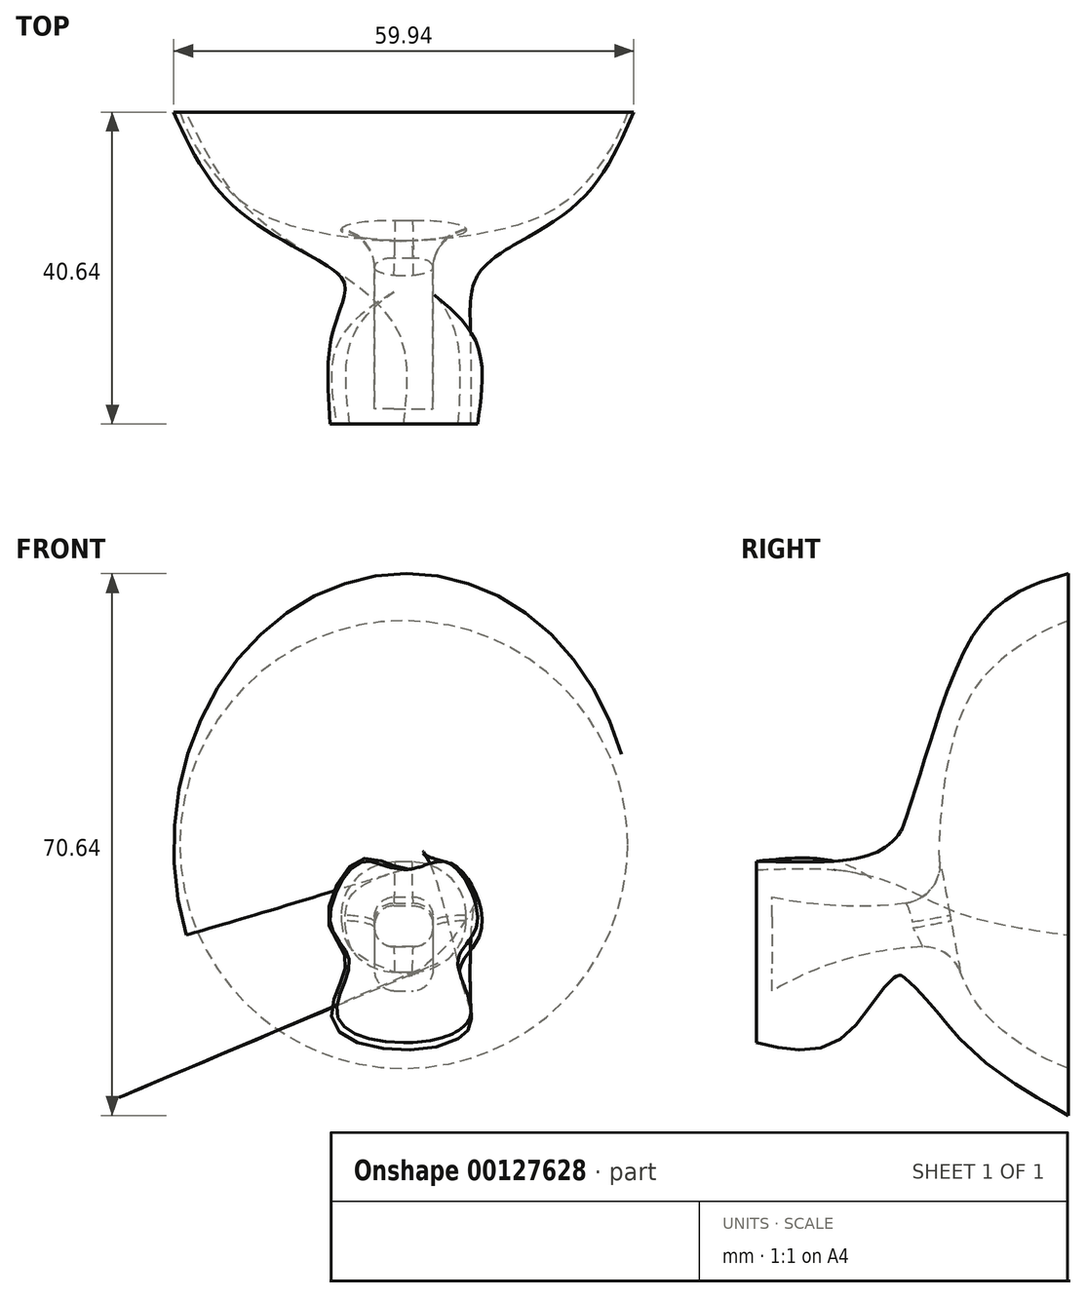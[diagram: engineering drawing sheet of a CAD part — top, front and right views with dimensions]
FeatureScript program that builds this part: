
annotation { "Feature Type Name" : "Feature", "Feature Type Description" : "" }
export const myFeature = defineFeature(function(context is Context, id is Id, definition is map)
    precondition{}
    {
        {
            var Q0;
            Q0=qCreatedBy(makeId("Front.planeOp"),FACE);
            var sketch = newSketch(context, id + "F0", { "sketchPlane" : qUnion([Q0])});
            skEllipse(sketch, "E0", {"center": v(0, 0) * mm, "majorRadius": 35.33 * mm, "minorRadius": 29.97 * mm, "majorAxis": v(0.03, 1)});
            skSolve(sketch);
        }
        {
            var Q0;
            Q0=qCreatedBy(makeId("Front.planeOp"),FACE);
            cPlane(context, id + "F1", {"entities" : qUnion([Q0]), "cplaneType" : CPlaneType.OFFSET, "offset" : 40.64 * mm, "width" : 152.4 * mm, "height" : 152.4 * mm});
        }
        {
            var Q0;
            Q0=qCreatedBy(makeId("Front.planeOp"),FACE);
            cPlane(context, id + "F2", {"entities" : qUnion([Q0]), "cplaneType" : CPlaneType.OFFSET, "offset" : 30.48 * mm, "width" : 152.4 * mm, "height" : 152.4 * mm});
        }
        {
            var Q0;
            Q0=qCreatedBy(id+"F1.planeOp",FACE);
            var sketch = newSketch(context, id + "F3", { "sketchPlane" : qUnion([Q0])});
            skFitSpline(sketch, "E1", {"points": [v(0, -3.28) * mm, v(-5.7, -2.35) * mm, v(-9.56, -10.3) * mm, v(-7.07, -15.2) * mm, v(-8.7, -22.25) * mm, v(0, -25.84) * mm], "startDerivative": vector(-42.07, 0) * mm, "endDerivative": vector(54.77, 0) * mm});
            skFitSpline(sketch, "E2.MirrorCS", {"points": [v(0, -3.28) * mm, v(5.7, -2.35) * mm, v(9.56, -10.3) * mm, v(7.07, -15.2) * mm, v(8.7, -22.25) * mm, v(0, -25.84) * mm], "startDerivative": vector(42.07, 0) * mm, "endDerivative": vector(-54.77, 0) * mm});
            skSolve(sketch);
        }
        {
            var Q0;
            Q0=qCreatedBy(id+"F2.planeOp",FACE);
            var sketch = newSketch(context, id + "F4", { "sketchPlane" : qUnion([Q0])});
            skFitSpline(sketch, "E3", {"points": [v(0, -3.28) * mm, v(-5.7, -2.35) * mm, v(-9.56, -10.3) * mm, v(-7.07, -15.2) * mm, v(-8.7, -22.25) * mm, v(0, -25.84) * mm], "startDerivative": vector(-33.29, 0) * mm, "endDerivative": vector(57.9, 0) * mm});
            skFitSpline(sketch, "E4.MirrorCS", {"points": [v(0, -3.28) * mm, v(5.7, -2.35) * mm, v(9.56, -10.3) * mm, v(7.07, -15.2) * mm, v(8.7, -22.25) * mm, v(0, -25.84) * mm], "startDerivative": vector(33.29, 0) * mm, "endDerivative": vector(-57.9, 0) * mm});
            skSolve(sketch);
        }
        {
            var Q0;
            Q0=qCreatedBy(makeId("Front.planeOp"),FACE);
            cPlane(context, id + "F5", {"entities" : qUnion([Q0]), "cplaneType" : CPlaneType.OFFSET, "offset" : 12.7 * mm, "width" : 152.4 * mm, "height" : 152.4 * mm});
        }
        {
            var Q0;
            Q0=qCreatedBy(id+"F5.planeOp",FACE);
            var sketch = newSketch(context, id + "F6", { "sketchPlane" : qUnion([Q0])});
            skEllipse(sketch, "E5", {"center": v(0, 0) * mm, "majorRadius": 26.8 * mm, "minorRadius": 21.66 * mm, "majorAxis": v(0, -1)});
            skSolve(sketch);
        }
        {
            var Q0;
            Q0=makeQuery(id+"F3.imprint","IMPRINT",FACE,{"disambiguationData":[TD([[makeQuery(id+"F3.imprint","IMPRINT",EDGE,{"derivedFrom":sQuery(id+"F3.wireOp",EDGE,"E1")}),1.0]])]});
            var Q1;
            Q1=makeQuery(id+"F4.imprint","IMPRINT",FACE,{"disambiguationData":[TD([[makeQuery(id+"F4.imprint","IMPRINT",EDGE,{"derivedFrom":sQuery(id+"F4.wireOp",EDGE,"E3")}),1.0]])]});
            var Q2;
            Q2=makeQuery(id+"F6.imprint","IMPRINT",FACE,{"disambiguationData":[TD([[makeQuery(id+"F6.imprint","IMPRINT",EDGE,{"derivedFrom":sQuery(id+"F6.wireOp",EDGE,"E5")}),1.0]])]});
            var Q3;
            Q3=makeQuery(id+"F0.imprint","IMPRINT",FACE,{"disambiguationData":[TD([[makeQuery(id+"F0.imprint","IMPRINT",EDGE,{"derivedFrom":sQuery(id+"F0.wireOp",EDGE,"E0")}),1.0]])]});
            loft(context, id + "F7", {"sheetProfilesArray" : [{ "sheetProfileEntities" : qUnion([Q0]) }, { "sheetProfileEntities" : qUnion([Q1]) }, { "sheetProfileEntities" : qUnion([Q2]) }, { "sheetProfileEntities" : qUnion([Q3]) }]});
        }
        {
            var Q0;
            Q0=qCreatedBy(makeId("Right.planeOp"),FACE);
            var sketch = newSketch(context, id + "F8", { "sketchPlane" : qUnion([Q0])});
            skLineSegment(sketch, "E6", {"start": v(0, 0) * mm, "end": v(0, -29.18) * mm});
            skFitSpline(sketch, "E7", {"points": [v(0, -29.18) * mm, v(-8.76, -24.06) * mm, v(-13.51, -18) * mm, v(-16.88, 0) * mm], "startDerivative": vector(-35.54, 13) * mm, "endDerivative": vector(-2.07, 53.83) * mm});
            skLineSegment(sketch, "E8", {"start": v(0, 0) * mm, "end": v(-16.88, 0) * mm});
            skSolve(sketch);
        }
        {
            var Q0;
            Q0 = qSketchRegion(id + "F8", true);
            var Q1;
            Q1=sQuery(id+"F8.wireOp",EDGE,"E8");
            revolve(context, id + "F9", {"operationType" : NewBodyOperationType.REMOVE, "entities" : qUnion([Q0]), "axis" : qUnion([Q1]), "revolveType" : RevolveType.FULL, "oppositeDirection" : true});
        }
        {
            var Q0;
            Q0=qCreatedBy(makeId("Right.planeOp"),FACE);
            var sketch = newSketch(context, id + "F10", { "sketchPlane" : qUnion([Q0])});
            skLineSegment(sketch, "E9", {"start": v(-15.66, -13.34) * mm, "end": v(-16.33, -6.83) * mm});
            skArc(sketch, "E10", {"start": v(-38.64, -6.83) * mm, "mid": v(-27.49, -7.99) * mm, "end": v(-16.33, -6.83) * mm});
            skPoint(sketch, "E11", {"position": v(-27.49, -7.99) * mm});
            skLineSegment(sketch, "E12", {"start": v(-16.33, -6.83) * mm, "end": v(-27.49, -7.99) * mm, "construction": true});
            skArc(sketch, "E13", {"start": v(-15.66, -13.34) * mm, "mid": v(-27.57, -14.57) * mm, "end": v(-38.64, -19.11) * mm});
            skPoint(sketch, "E14", {"position": v(-27.57, -14.57) * mm});
            skLineSegment(sketch, "E15", {"start": v(-15.66, -13.34) * mm, "end": v(-27.57, -14.57) * mm, "construction": true});
            skLineSegment(sketch, "E16", {"start": v(-38.64, -6.83) * mm, "end": v(-38.64, -19.11) * mm});
            skArc(sketch, "E17", {"start": v(-15.66, -13.34) * mm, "mid": v(-12.74, -9.75) * mm, "end": v(-16.33, -6.83) * mm});
            skSolve(sketch);
        }
        {
            var Q0;
            Q0 = qSketchRegion(id + "F10", true);
            extrude(context, id + "F11", {"entities" : qUnion([Q0]), "operationType" : NewBodyOperationType.REMOVE, "oppositeDirection" : true, "depth" : 3.8 * mm, "hasSecondDirection" : true, "secondDirectionOppositeDirection" : false, "secondDirectionDepth" : 3.8 * mm});
        }
        {
            var Q0;
            Q0=makeQuery(id+"F11.boolean.opBoolean","COPY",EDGE,{"derivedFrom":makeQuery(id+"F11.opExtrude","CAP_EDGE",EDGE,{"disambiguationData":[OSD([sQuery(id+"F10.wireOp",EDGE,"E10")])],"isStart":false})});
            var Q1;
            Q1=makeQuery(id+"F11.boolean.opBoolean","COPY",EDGE,{"derivedFrom":makeQuery(id+"F11.opExtrude","CAP_EDGE",EDGE,{"disambiguationData":[OSD([sQuery(id+"F10.wireOp",EDGE,"E10")])],"isStart":true})});
            var Q2;
            Q2=makeQuery(id+"F11.boolean.opBoolean","COPY",EDGE,{"derivedFrom":makeQuery(id+"F11.opExtrude","CAP_EDGE",EDGE,{"disambiguationData":[OSD([sQuery(id+"F10.wireOp",EDGE,"E13")])],"isStart":true})});
            var Q3;
            Q3=makeQuery(id+"F11.boolean.opBoolean","COPY",EDGE,{"derivedFrom":makeQuery(id+"F11.opExtrude","CAP_EDGE",EDGE,{"disambiguationData":[OSD([sQuery(id+"F10.wireOp",EDGE,"E13")])],"isStart":false})});
            fillet(context, id + "F12", {"entities" : qUnion([Q0, Q1, Q2, Q3]), "radius" : 2.54 * mm, "tangentPropagation" : true, "allowEdgeOverflow" : false});
        }
        {
            var Q0;
            Q0=makeQuery(id+"F11.boolean.opBoolean","INTERSECT",EDGE,{"derivedFrom":[makeQuery(id+"F9.boolean.opBoolean","COPY",FACE,{"derivedFrom":makeQuery(id+"F9.opRevolve","SWEPT_FACE",FACE,{"disambiguationData":[OSD([sQuery(id+"F8.wireOp",EDGE,"E7")])]})}),makeQuery(id+"F11.opExtrude","CAP_FACE",FACE,{"disambiguationData":[OSD([sQuery(id+"F10.wireOp",EDGE,"E10"),sQuery(id+"F10.wireOp",EDGE,"E13"),sQuery(id+"F10.wireOp",EDGE,"E16"),sQuery(id+"F10.wireOp",EDGE,"E17")])],"isStart":false})]});
            var Q1;
            Q1=makeQuery(id+"F12.opFillet","BLEND_EDGE",EDGE,{"blendedFrom":[makeQuery(id+"F11.boolean.opBoolean","COPY",EDGE,{"derivedFrom":makeQuery(id+"F11.opExtrude","CAP_EDGE",EDGE,{"disambiguationData":[OSD([sQuery(id+"F10.wireOp",EDGE,"E13")])],"isStart":false})}),makeQuery(id+"F9.boolean.opBoolean","COPY",FACE,{"derivedFrom":makeQuery(id+"F9.opRevolve","SWEPT_FACE",FACE,{"disambiguationData":[OSD([sQuery(id+"F8.wireOp",EDGE,"E7")])]})})],"blendedInto":[makeQuery(id+"F9.boolean.opBoolean","COPY",FACE,{"derivedFrom":makeQuery(id+"F9.opRevolve","SWEPT_FACE",FACE,{"disambiguationData":[OSD([sQuery(id+"F8.wireOp",EDGE,"E7")])]})})]});
            var Q2;
            Q2=makeQuery(id+"F11.boolean.opBoolean","INTERSECT",EDGE,{"disambiguationData":[OD(0.0)],"derivedFrom":[makeQuery(id+"F9.boolean.opBoolean","COPY",FACE,{"derivedFrom":makeQuery(id+"F9.opRevolve","SWEPT_FACE",FACE,{"disambiguationData":[OSD([sQuery(id+"F8.wireOp",EDGE,"E7")])]})}),makeQuery(id+"F11.opExtrude","SWEPT_FACE",FACE,{"disambiguationData":[OSD([sQuery(id+"F10.wireOp",EDGE,"E17")])]})]});
            var Q3;
            Q3=makeQuery(id+"F12.opFillet","BLEND_EDGE",EDGE,{"blendedFrom":[makeQuery(id+"F11.boolean.opBoolean","COPY",EDGE,{"derivedFrom":makeQuery(id+"F11.opExtrude","CAP_EDGE",EDGE,{"disambiguationData":[OSD([sQuery(id+"F10.wireOp",EDGE,"E13")])],"isStart":true})}),makeQuery(id+"F9.boolean.opBoolean","COPY",FACE,{"derivedFrom":makeQuery(id+"F9.opRevolve","SWEPT_FACE",FACE,{"disambiguationData":[OSD([sQuery(id+"F8.wireOp",EDGE,"E7")])]})})],"blendedInto":[makeQuery(id+"F9.boolean.opBoolean","COPY",FACE,{"derivedFrom":makeQuery(id+"F9.opRevolve","SWEPT_FACE",FACE,{"disambiguationData":[OSD([sQuery(id+"F8.wireOp",EDGE,"E7")])]})})]});
            var Q4;
            Q4=makeQuery(id+"F11.boolean.opBoolean","INTERSECT",EDGE,{"derivedFrom":[makeQuery(id+"F9.boolean.opBoolean","COPY",FACE,{"derivedFrom":makeQuery(id+"F9.opRevolve","SWEPT_FACE",FACE,{"disambiguationData":[OSD([sQuery(id+"F8.wireOp",EDGE,"E7")])]})}),makeQuery(id+"F11.opExtrude","CAP_FACE",FACE,{"disambiguationData":[OSD([sQuery(id+"F10.wireOp",EDGE,"E10"),sQuery(id+"F10.wireOp",EDGE,"E13"),sQuery(id+"F10.wireOp",EDGE,"E16"),sQuery(id+"F10.wireOp",EDGE,"E17")])],"isStart":true})]});
            var Q5;
            Q5=makeQuery(id+"F11.boolean.opBoolean","INTERSECT",EDGE,{"disambiguationData":[OD(1.0)],"derivedFrom":[makeQuery(id+"F9.boolean.opBoolean","COPY",FACE,{"derivedFrom":makeQuery(id+"F9.opRevolve","SWEPT_FACE",FACE,{"disambiguationData":[OSD([sQuery(id+"F8.wireOp",EDGE,"E7")])]})}),makeQuery(id+"F11.opExtrude","SWEPT_FACE",FACE,{"disambiguationData":[OSD([sQuery(id+"F10.wireOp",EDGE,"E17")])]})]});
            var Q6;
            Q6=makeQuery(id+"F12.opFillet","BLEND_EDGE",EDGE,{"blendedFrom":[makeQuery(id+"F11.boolean.opBoolean","COPY",EDGE,{"derivedFrom":makeQuery(id+"F11.opExtrude","CAP_EDGE",EDGE,{"disambiguationData":[OSD([sQuery(id+"F10.wireOp",EDGE,"E10")])],"isStart":false})}),makeQuery(id+"F9.boolean.opBoolean","COPY",FACE,{"derivedFrom":makeQuery(id+"F9.opRevolve","SWEPT_FACE",FACE,{"disambiguationData":[OSD([sQuery(id+"F8.wireOp",EDGE,"E7")])]})})],"blendedInto":[makeQuery(id+"F9.boolean.opBoolean","COPY",FACE,{"derivedFrom":makeQuery(id+"F9.opRevolve","SWEPT_FACE",FACE,{"disambiguationData":[OSD([sQuery(id+"F8.wireOp",EDGE,"E7")])]})})]});
            var Q7;
            Q7=makeQuery(id+"F12.opFillet","BLEND_EDGE",EDGE,{"blendedFrom":[makeQuery(id+"F11.boolean.opBoolean","COPY",EDGE,{"derivedFrom":makeQuery(id+"F11.opExtrude","CAP_EDGE",EDGE,{"disambiguationData":[OSD([sQuery(id+"F10.wireOp",EDGE,"E10")])],"isStart":true})}),makeQuery(id+"F9.boolean.opBoolean","COPY",FACE,{"derivedFrom":makeQuery(id+"F9.opRevolve","SWEPT_FACE",FACE,{"disambiguationData":[OSD([sQuery(id+"F8.wireOp",EDGE,"E7")])]})})],"blendedInto":[makeQuery(id+"F9.boolean.opBoolean","COPY",FACE,{"derivedFrom":makeQuery(id+"F9.opRevolve","SWEPT_FACE",FACE,{"disambiguationData":[OSD([sQuery(id+"F8.wireOp",EDGE,"E7")])]})})]});
            fillet(context, id + "F13", {"entities" : qUnion([Q0, Q1, Q2, Q3, Q4, Q5, Q6, Q7]), "radius" : 5.08 * mm, "tangentPropagation" : true, "allowEdgeOverflow" : false});
        }
    });
